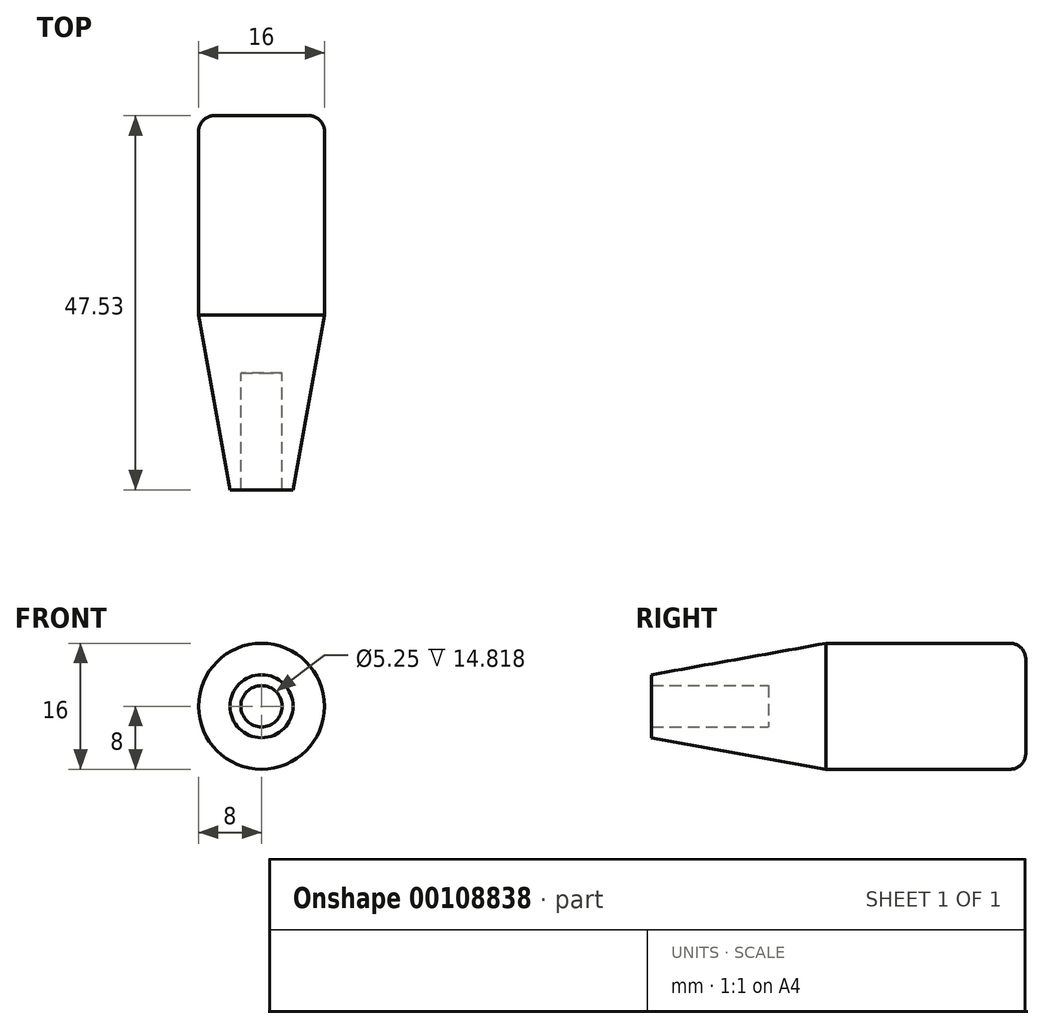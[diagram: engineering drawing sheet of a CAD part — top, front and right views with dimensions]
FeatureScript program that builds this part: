
annotation { "Feature Type Name" : "Feature", "Feature Type Description" : "" }
export const myFeature = defineFeature(function(context is Context, id is Id, definition is map)
    precondition{}
    {
        {
            var Q0;
            Q0=qCreatedBy(makeId("Top.planeOp"),FACE);
            var sketch = newSketch(context, id + "F0", { "sketchPlane" : qUnion([Q0])});
            skLineSegment(sketch, "E0", {"start": v(0, 32.71) * mm, "end": v(-8, 32.71) * mm});
            skLineSegment(sketch, "E1", {"start": v(-8, 32.71) * mm, "end": v(-8, 7.36) * mm});
            skLineSegment(sketch, "E2", {"start": v(-8, 7.36) * mm, "end": v(-4, -14.82) * mm});
            skLineSegment(sketch, "E3", {"start": v(-4, -14.82) * mm, "end": v(0, -14.82) * mm});
            skLineSegment(sketch, "E4", {"start": v(0, -14.82) * mm, "end": v(0, 32.71) * mm});
            skSolve(sketch);
        }
        {
            var Q0;
            Q0=qCreatedBy(makeId("Top.planeOp"),FACE);
            var sketch = newSketch(context, id + "F1", { "sketchPlane" : qUnion([Q0])});
            skLineSegment(sketch, "E5", {"start": v(0, 46.7) * mm, "end": v(0, -28.98) * mm, "construction": true});
            skSolve(sketch);
        }
        {
            var Q0;
            Q0=makeQuery(id+"F0.imprint","IMPRINT",FACE,{"disambiguationData":[TD([[makeQuery(id+"F0.imprint","IMPRINT",EDGE,{"derivedFrom":sQuery(id+"F0.wireOp",EDGE,"E0")}),1.0]])]});
            var Q1;
            Q1=sQuery(id+"F1.wireOp",EDGE,"E5");
            revolve(context, id + "F2", {"entities" : qUnion([Q0]), "axis" : qUnion([Q1]), "revolveType" : RevolveType.FULL});
        }
        {
            var Q0;
            Q0=makeQuery(id+"F2.opRevolve","SWEPT_EDGE",EDGE,{"disambiguationData":[OSD([sQuery(id+"F0.wireOp",EDGE,"E0"),sQuery(id+"F0.wireOp",EDGE,"E1")])]});
            fillet(context, id + "F3", {"entities" : qUnion([Q0]), "radius" : 2 * mm, "tangentPropagation" : true, "allowEdgeOverflow" : false});
        }
        {
            var Q0;
            Q0=qCreatedBy(makeId("Front.planeOp"),FACE);
            var sketch = newSketch(context, id + "F4", { "sketchPlane" : qUnion([Q0])});
            skLineSegment(sketch, "E6", {"start": v(-4.45, 0) * mm, "end": v(5.74, 0) * mm, "construction": true});
            skLineSegment(sketch, "E7", {"start": v(0, 4.48) * mm, "end": v(0, -3.3) * mm, "construction": true});
            skPoint(sketch, "E8", {"position": v(0, 0) * mm});
            skSolve(sketch);
        }
        {
            var Q0;
            Q0=sQuery(id+"F4.wireOp",VERTEX,"E8");
            var Q1;
            Q1=makeQuery(id+"F2.opRevolve","SWEPT_BODY",BODY,{"disambiguationData":[OSD([sQuery(id+"F0.wireOp",EDGE,"E0"),sQuery(id+"F0.wireOp",EDGE,"E1"),sQuery(id+"F0.wireOp",EDGE,"E2"),sQuery(id+"F0.wireOp",EDGE,"E3"),sQuery(id+"F0.wireOp",EDGE,"E4")])]});
            hole(context, id + "F5", {"style" : HoleStyle.SIMPLE, "endStyle" : HoleEndStyle.THROUGH, "oppositeDirection" : true, "standardTappedOrClearance" : lookupTablePath({ "standard" : "ISO", "fit" : "Close", "size" : "M5", "type" : "Clearance" }), "standardBlindInLast" : lookupTablePath({ "fit" : "Close", "standard" : "ISO", "size" : "M5", "type" : "Clearance" }), "holeDiameter" : 5.25 * mm, "startFromSketch" : true, "locations" : qUnion([Q0]), "scope" : qUnion([Q1]), "isTappedThrough" : true});
        }
        {
            var Q0;
            Q0=makeQuery(id+"F2.opRevolve","SWEPT_BODY",BODY,{"disambiguationData":[OSD([sQuery(id+"F0.wireOp",EDGE,"E0"),sQuery(id+"F0.wireOp",EDGE,"E1"),sQuery(id+"F0.wireOp",EDGE,"E2"),sQuery(id+"F0.wireOp",EDGE,"E3"),sQuery(id+"F0.wireOp",EDGE,"E4")])]});
            transform(context, id + "F6", {"entities" : qUnion([Q0]), "transformType" : TransformType.TRANSLATION_3D, "dx" : 8 * mm, "dy" : 0 * mm, "dz" : 0 * mm, "makeCopy" : false});
        }
    });
